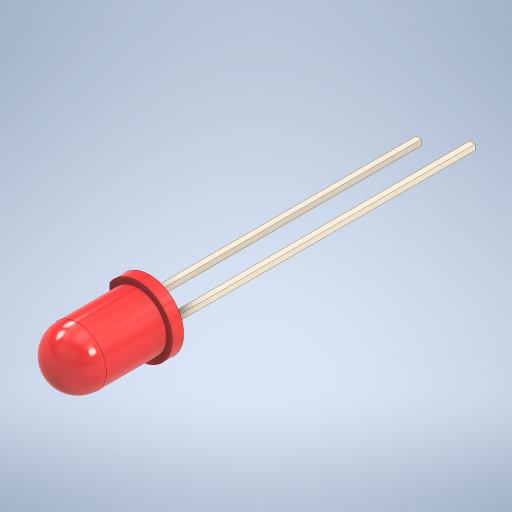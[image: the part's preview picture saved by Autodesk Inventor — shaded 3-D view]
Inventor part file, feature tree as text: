
AUTODESK INVENTOR PART (.ipt)
format: ipt  version: 2023 (Build 270158000, 158)  size: 302,592 bytes
history: imported  units: in
note: dims shown in document units (in); Inventor stores cm internally (conversion verified against a paired STEP export)
features: imported_body x1
ambient origin geometry x8: Origin, YZ Plane, XZ Plane, XY Plane, X Axis, Y Axis, Z Axis, Center Point
bodies: Solid1 (imported_parasolid), Solid2 (imported_parasolid), Solid3 (imported_parasolid), Body1 (imported_parasolid), Body2 (imported_parasolid), Body3 (imported_parasolid)
feature tree (1):
  imported_body  NMx_Import_Brep_tag  [imported B-rep: ~42 faces, bbox_mm=[4.1, 4.158312, 33.3]]
